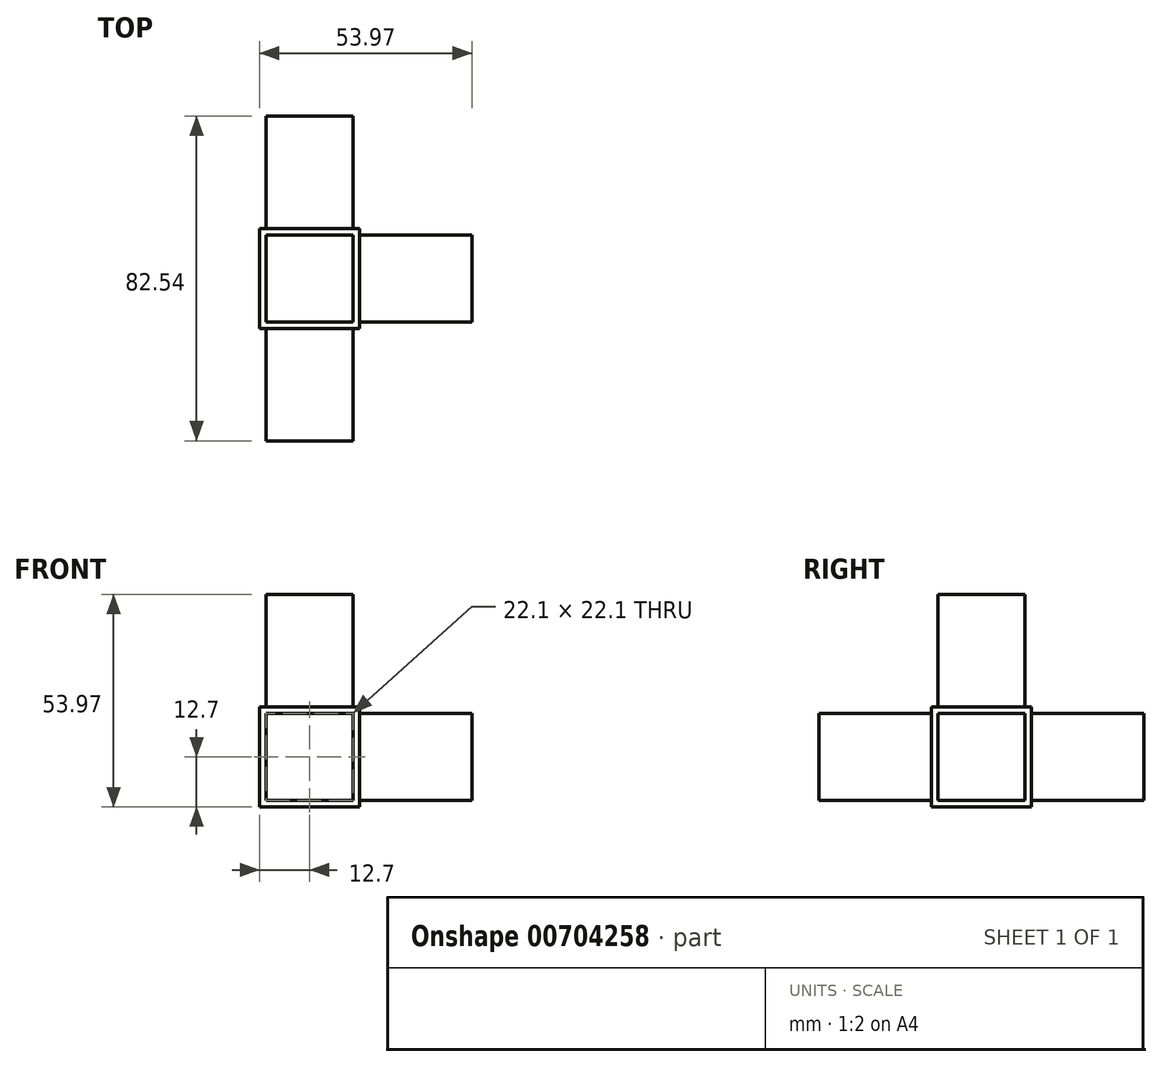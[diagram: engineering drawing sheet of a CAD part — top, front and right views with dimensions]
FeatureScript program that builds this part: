
annotation { "Feature Type Name" : "Feature", "Feature Type Description" : "" }
export const myFeature = defineFeature(function(context is Context, id is Id, definition is map)
    precondition{}
    {
        {
            var Q0;
            Q0=qCreatedBy(makeId("Front.planeOp"),FACE);
            var sketch = newSketch(context, id + "F0", { "sketchPlane" : qUnion([Q0])});
            skLineSegment(sketch, "E0.bottom", {"start": v(-12.7, 12.7) * mm, "end": v(12.7, 12.7) * mm});
            skLineSegment(sketch, "E0.top", {"start": v(-12.7, -12.7) * mm, "end": v(12.7, -12.7) * mm});
            skLineSegment(sketch, "E0.left", {"start": v(-12.7, 12.7) * mm, "end": v(-12.7, -12.7) * mm});
            skLineSegment(sketch, "E0.right", {"start": v(12.7, 12.7) * mm, "end": v(12.7, -12.7) * mm});
            skPoint(sketch, "E0.middle", {"position": v(0, 0) * mm});
            skLineSegment(sketch, "E1", {"start": v(-11.05, 12.7) * mm, "end": v(-11.05, 41.28) * mm});
            skLineSegment(sketch, "E2", {"start": v(-11.05, 41.28) * mm, "end": v(11.05, 41.28) * mm});
            skLineSegment(sketch, "E3", {"start": v(11.05, 41.28) * mm, "end": v(11.05, 12.7) * mm});
            skLineSegment(sketch, "E4", {"start": v(12.7, 11.05) * mm, "end": v(41.27, 11.05) * mm});
            skLineSegment(sketch, "E5", {"start": v(41.27, 11.05) * mm, "end": v(41.27, -11.05) * mm});
            skLineSegment(sketch, "E6", {"start": v(41.27, -11.05) * mm, "end": v(12.7, -11.05) * mm});
            skLineSegment(sketch, "E7.bottom", {"start": v(-11.05, 11.05) * mm, "end": v(11.05, 11.05) * mm});
            skLineSegment(sketch, "E7.top", {"start": v(-11.05, -11.05) * mm, "end": v(11.05, -11.05) * mm});
            skLineSegment(sketch, "E7.left", {"start": v(-11.05, 11.05) * mm, "end": v(-11.05, -11.05) * mm});
            skLineSegment(sketch, "E7.right", {"start": v(11.05, 11.05) * mm, "end": v(11.05, -11.05) * mm});
            skSolve(sketch);
        }
        {
            var Q0;
            Q0=makeQuery(id+"F0.imprint","IMPRINT",FACE,{"disambiguationData":[TD([[makeQuery(id+"F0.imprint","IMPRINT",EDGE,{"derivedFrom":sQuery(id+"F0.wireOp",EDGE,"E7.bottom")}),-1.0]])]});
            extrude(context, id + "F1", {"entities" : qUnion([Q0]), "endBound" : BoundingType.SYMMETRIC, "depth" : 82.55 * mm, "offsetDistance" : 25.4 * mm});
        }
        {
            var Q0;
            {var subQ1=sQuery(id+"F0.wireOp",EDGE,"E0.top");Q0=makeQuery(id+"F0.imprint","IMPRINT",FACE,{"disambiguationData":[TD([[makeQuery(id+"F0.imprint","IMPRINT",EDGE,{"derivedFrom":subQ1}),1.0]])]});}
            var Q1;
            Q1=makeQuery(id+"F0.imprint","IMPRINT",FACE,{"disambiguationData":[TD([[makeQuery(id+"F0.imprint","IMPRINT",EDGE,{"derivedFrom":sQuery(id+"F0.wireOp",EDGE,"E7.bottom")}),-1.0]])]});
            extrude(context, id + "F2", {"entities" : qUnion([Q0, Q1]), "operationType" : NewBodyOperationType.ADD, "endBound" : BoundingType.SYMMETRIC, "depth" : 25.4 * mm, "offsetDistance" : 25.4 * mm});
        }
        {
            var Q0;
            {var subQ0=sQuery(id+"F0.wireOp",EDGE,"E1");Q0=makeQuery(id+"F0.imprint","IMPRINT",FACE,{"disambiguationData":[TD([[makeQuery(id+"F0.imprint","IMPRINT",EDGE,{"derivedFrom":subQ0}),-1.0]])]});}
            extrude(context, id + "F3", {"entities" : qUnion([Q0]), "operationType" : NewBodyOperationType.ADD, "endBound" : BoundingType.SYMMETRIC, "depth" : 22.1 * mm, "offsetDistance" : 25.4 * mm});
        }
        {
            var Q0;
            {var subQ0=sQuery(id+"F0.wireOp",EDGE,"E4");Q0=makeQuery(id+"F0.imprint","IMPRINT",FACE,{"disambiguationData":[TD([[makeQuery(id+"F0.imprint","IMPRINT",EDGE,{"derivedFrom":subQ0}),-1.0]])]});}
            extrude(context, id + "F4", {"entities" : qUnion([Q0]), "operationType" : NewBodyOperationType.ADD, "endBound" : BoundingType.SYMMETRIC, "depth" : 22.1 * mm, "offsetDistance" : 25.4 * mm});
        }
    });
